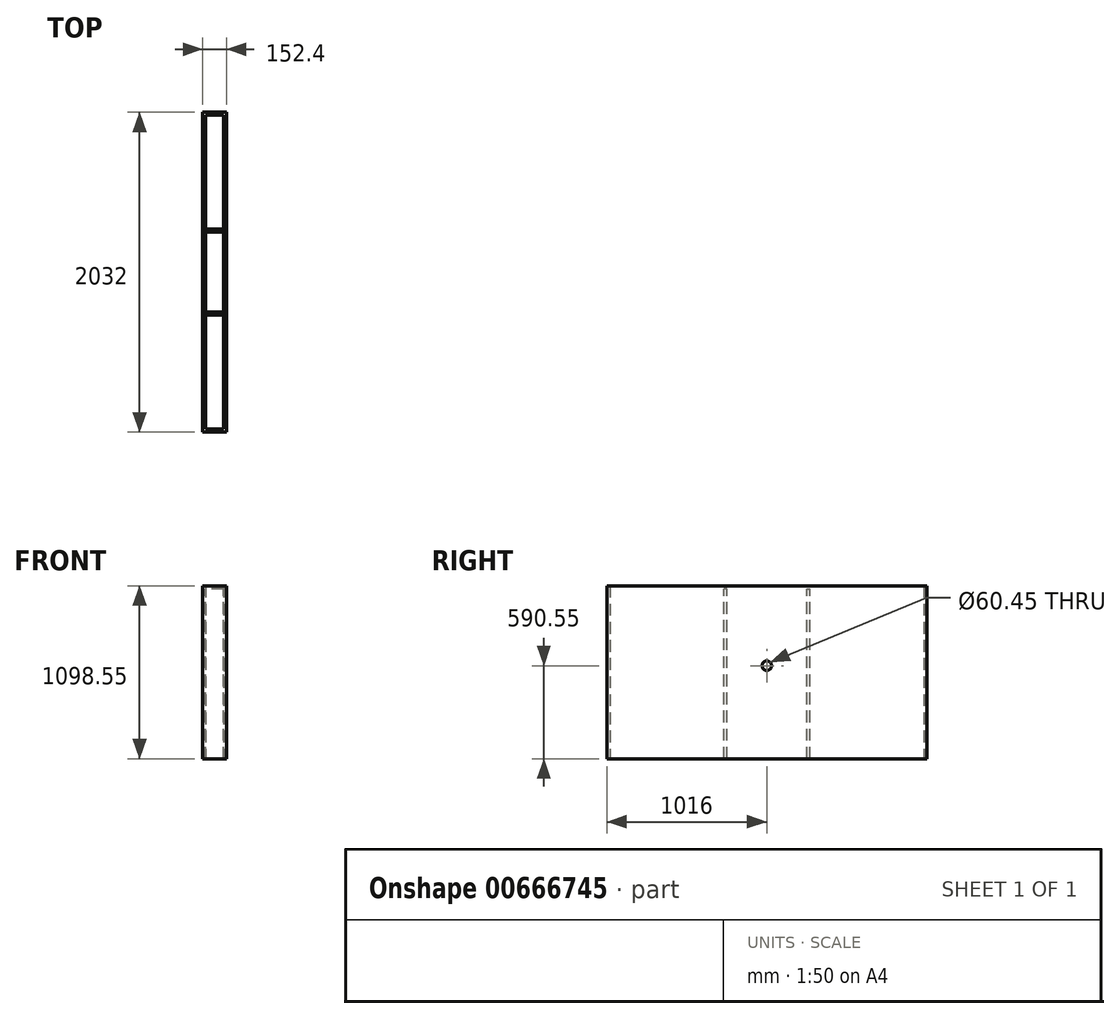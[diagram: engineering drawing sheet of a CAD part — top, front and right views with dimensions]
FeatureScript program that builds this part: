
annotation { "Feature Type Name" : "Feature", "Feature Type Description" : "" }
export const myFeature = defineFeature(function(context is Context, id is Id, definition is map)
    precondition{}
    {
        {
            var Q0;
            Q0=qCreatedBy(makeId("Top.planeOp"),FACE);
            var sketch = newSketch(context, id + "F0", { "sketchPlane" : qUnion([Q0])});
            skLineSegment(sketch, "E0.bottom", {"start": v(76.2, 1016) * mm, "end": v(-76.2, 1016) * mm});
            skLineSegment(sketch, "E0.top", {"start": v(76.2, -1016) * mm, "end": v(-76.2, -1016) * mm});
            skLineSegment(sketch, "E0.left", {"start": v(76.2, 1016) * mm, "end": v(76.2, -1016) * mm});
            skLineSegment(sketch, "E0.right", {"start": v(-76.2, 1016) * mm, "end": v(-76.2, -1016) * mm});
            skPoint(sketch, "E0.middle", {"position": v(0, 0) * mm});
            skLineSegment(sketch, "E1.bottom", {"start": v(57.15, 996.95) * mm, "end": v(-57.15, 996.95) * mm});
            skLineSegment(sketch, "E1.top", {"start": v(57.15, -996.95) * mm, "end": v(-57.15, -996.95) * mm});
            skLineSegment(sketch, "E1.left", {"start": v(57.15, 996.95) * mm, "end": v(57.15, -996.95) * mm});
            skLineSegment(sketch, "E1.right", {"start": v(-57.15, 996.95) * mm, "end": v(-57.15, -996.95) * mm});
            skSolve(sketch);
        }
        {
            var Q0;
            Q0=makeQuery(id+"F0.imprint","IMPRINT",FACE,{"disambiguationData":[TD([[makeQuery(id+"F0.imprint","IMPRINT",EDGE,{"derivedFrom":sQuery(id+"F0.wireOp",EDGE,"E0.bottom")}),1.0]])]});
            extrude(context, id + "F1", {"entities" : qUnion([Q0]), "depth" : 1098.55 * mm, "offsetDistance" : 25.4 * mm});
        }
        {
            var Q0;
            Q0=makeQuery(id+"F1.opExtrude","SWEPT_FACE",FACE,{"disambiguationData":[OSD([sQuery(id+"F0.wireOp",EDGE,"E0.left")])]});
            var sketch = newSketch(context, id + "F2", { "sketchPlane" : qUnion([Q0])});
            skLineSegment(sketch, "E2", {"start": v(0, 1098.55) * mm, "end": v(0, 590.55) * mm});
            skCircle(sketch, "E3", {"center": v(0, 590.55) * mm, "radius": 30.23 * mm});
            skSolve(sketch);
        }
        {
            var Q0;
            Q0=makeQuery(id+"F2.imprint","IMPRINT",FACE,{"disambiguationData":[TD([[makeQuery(id+"F2.imprint","IMPRINT",EDGE,{"derivedFrom":sQuery(id+"F2.wireOp",EDGE,"E3")}),1.0]])]});
            extrude(context, id + "F3", {"entities" : qUnion([Q0]), "operationType" : NewBodyOperationType.REMOVE, "oppositeDirection" : true, "depth" : 25.4 * mm, "offsetDistance" : 25.4 * mm});
        }
        {
            var Q0;
            Q0=makeQuery(id+"F1.opExtrude","SWEPT_FACE",FACE,{"disambiguationData":[OSD([sQuery(id+"F0.wireOp",EDGE,"E1.right")])]});
            var sketch = newSketch(context, id + "F4", { "sketchPlane" : qUnion([Q0])});
            skLineSegment(sketch, "E4", {"start": v(0, 0) * mm, "end": v(254, 0) * mm});
            skLineSegment(sketch, "E5.bottom", {"start": v(254, 0) * mm, "end": v(273.05, 0) * mm});
            skLineSegment(sketch, "E5.top", {"start": v(254, 1079.5) * mm, "end": v(273.05, 1079.5) * mm});
            skLineSegment(sketch, "E5.left", {"start": v(254, 0) * mm, "end": v(254, 1079.5) * mm});
            skLineSegment(sketch, "E5.right", {"start": v(273.05, 0) * mm, "end": v(273.05, 1079.5) * mm});
            skLineSegment(sketch, "E6", {"start": v(0, 0) * mm, "end": v(-254, 0) * mm});
            skLineSegment(sketch, "E7.bottom", {"start": v(-254, 0) * mm, "end": v(-273.05, 0) * mm});
            skLineSegment(sketch, "E7.top", {"start": v(-254, 1079.5) * mm, "end": v(-273.05, 1079.5) * mm});
            skLineSegment(sketch, "E7.left", {"start": v(-254, 0) * mm, "end": v(-254, 1079.5) * mm});
            skLineSegment(sketch, "E7.right", {"start": v(-273.05, 0) * mm, "end": v(-273.05, 1079.5) * mm});
            skSolve(sketch);
        }
        {
            var Q0;
            Q0=makeQuery(id+"F4.imprint","IMPRINT",FACE,{"disambiguationData":[TD([[makeQuery(id+"F4.imprint","IMPRINT",EDGE,{"derivedFrom":sQuery(id+"F4.wireOp",EDGE,"E7.bottom")}),-1.0]])]});
            var Q1;
            Q1=makeQuery(id+"F4.imprint","IMPRINT",FACE,{"disambiguationData":[TD([[makeQuery(id+"F4.imprint","IMPRINT",EDGE,{"derivedFrom":sQuery(id+"F4.wireOp",EDGE,"E5.bottom")}),-1.0]])]});
            extrude(context, id + "F5", {"entities" : qUnion([Q0, Q1]), "operationType" : NewBodyOperationType.ADD, "depth" : 114.3 * mm, "offsetDistance" : 25.4 * mm});
        }
    });
